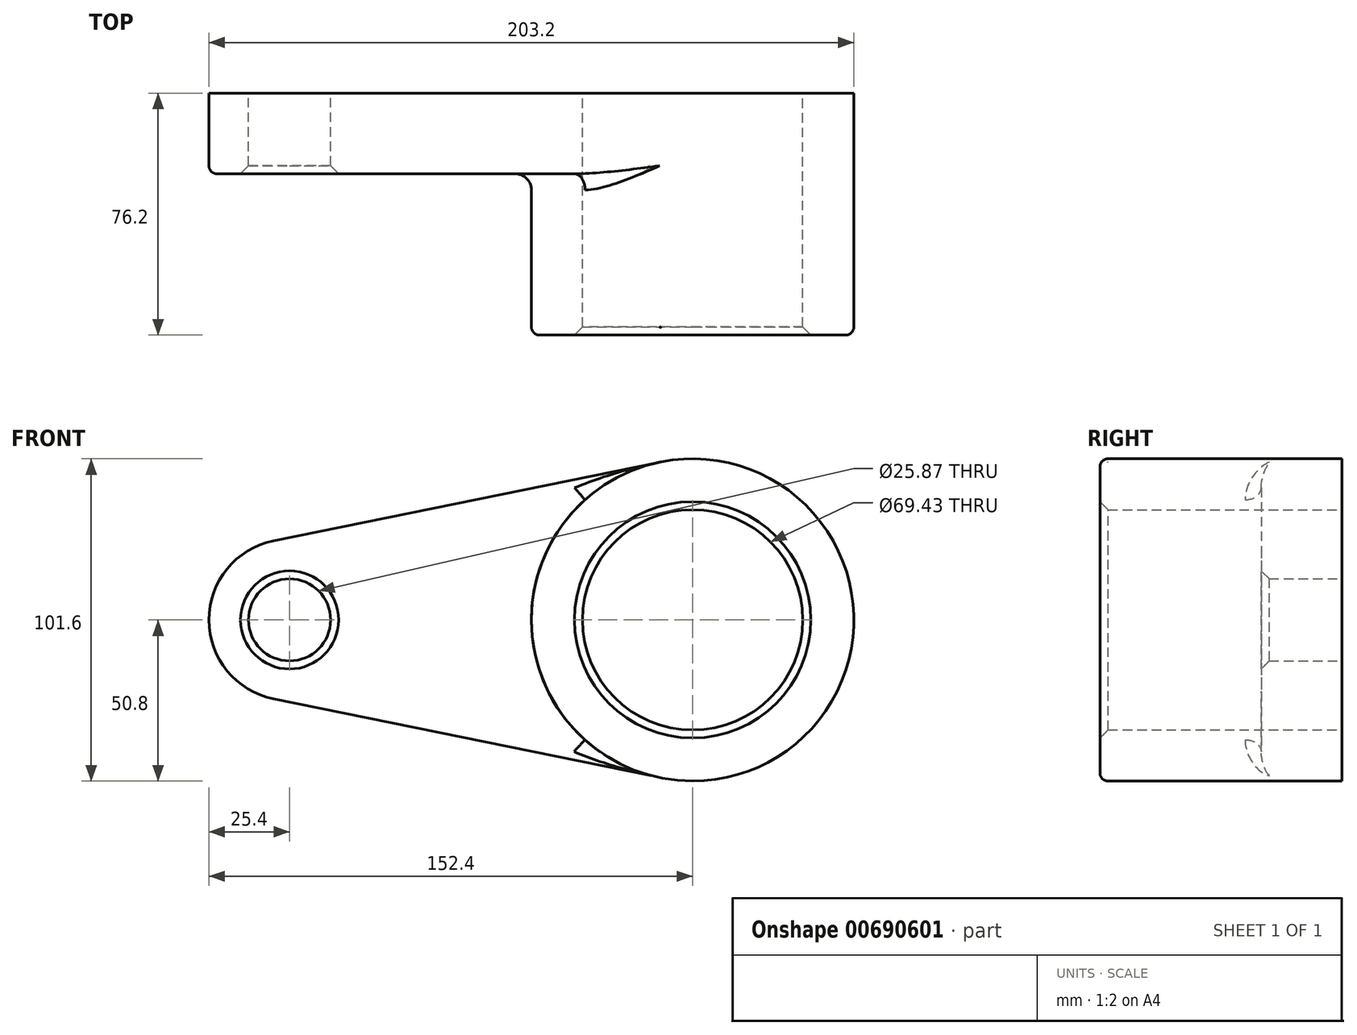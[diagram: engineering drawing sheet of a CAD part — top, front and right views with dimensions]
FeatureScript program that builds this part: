
annotation { "Feature Type Name" : "Feature", "Feature Type Description" : "" }
export const myFeature = defineFeature(function(context is Context, id is Id, definition is map)
    precondition{}
    {
        {
            var Q0;
            Q0=qCreatedBy(makeId("Front.planeOp"),FACE);
            var sketch = newSketch(context, id + "F0", { "sketchPlane" : qUnion([Q0])});
            skCircle(sketch, "E0", {"center": v(0, 0) * mm, "radius": 50.8 * mm});
            skCircle(sketch, "E1", {"center": v(-127, 0) * mm, "radius": 25.4 * mm});
            skLineSegment(sketch, "E2", {"start": v(-13.3, -49.03) * mm, "end": v(-132.06, -24.9) * mm});
            skLineSegment(sketch, "E3", {"start": v(-9.88, 49.83) * mm, "end": v(-132.08, 24.89) * mm});
            skCircle(sketch, "E4", {"center": v(0, 0) * mm, "radius": 34.71 * mm});
            skCircle(sketch, "E5", {"center": v(-127, 0) * mm, "radius": 12.94 * mm});
            skSolve(sketch);
        }
        {
            var Q0;
            Q0 = qSketchRegion(id + "F0", true);
            extrude(context, id + "F1", {"entities" : qUnion([Q0]), "depth" : 25.4 * mm, "offsetDistance" : 25.4 * mm});
        }
        {
            var Q0;
            Q0 = qSketchRegion(id + "F0", true);
            extrude(context, id + "F2", {"entities" : qUnion([Q0]), "operationType" : NewBodyOperationType.REMOVE, "oppositeDirection" : true, "depth" : 76.2 * mm, "offsetDistance" : 25.4 * mm});
        }
        {
            var Q0;
            Q0=makeQuery(id+"F0.imprint","IMPRINT",FACE,{"disambiguationData":[TD([[makeQuery(id+"F0.imprint","IMPRINT",EDGE,{"derivedFrom":sQuery(id+"F0.wireOp",EDGE,"E4")}),-1.0]])]});
            extrude(context, id + "F3", {"entities" : qUnion([Q0]), "operationType" : NewBodyOperationType.ADD, "depth" : 76.2 * mm, "offsetDistance" : 25.4 * mm});
        }
        {
            var Q0;
            Q0=makeQuery(id+"F3.opExtrude","CAP_EDGE",EDGE,{"disambiguationData":[OSD([sQuery(id+"F0.wireOp",EDGE,"E0")])],"isStart":false});
            fillet(context, id + "F4", {"entities" : qUnion([Q0]), "radius" : 2.54 * mm, "tangentPropagation" : true, "allowEdgeOverflow" : false});
        }
        {
            var Q0;
            Q0=makeQuery(id+"F3.opExtrude","CAP_EDGE",EDGE,{"disambiguationData":[OSD([sQuery(id+"F0.wireOp",EDGE,"E4")])],"isStart":false});
            chamfer(context, id + "F5", {"entities" : qUnion([Q0]), "width" : 2.54 * mm, "tangentPropagation" : true});
        }
        {
            var Q0;
            Q0=makeQuery(id+"F1.opExtrude","CAP_EDGE",EDGE,{"disambiguationData":[OSD([sQuery(id+"F0.wireOp",EDGE,"E5")])],"isStart":false});
            chamfer(context, id + "F6", {"entities" : qUnion([Q0]), "width" : 2.54 * mm, "tangentPropagation" : true});
        }
        {
            var Q0;
            Q0=makeQuery(id+"F1.opExtrude","CAP_EDGE",EDGE,{"disambiguationData":[OSD([sQuery(id+"F0.wireOp",EDGE,"E3")])],"isStart":false});
            fillet(context, id + "F7", {"entities" : qUnion([Q0]), "radius" : 2.54 * mm, "tangentPropagation" : true, "allowEdgeOverflow" : false});
        }
        {
            var Q0;
            {var subQ0=sQuery(id+"F0.wireOp",EDGE,"E0");Q0=makeQuery(id+"F3.boolean.opBoolean","INTERSECT",EDGE,{"derivedFrom":[makeQuery(id+"F1.opExtrude","CAP_FACE",FACE,{"disambiguationData":[OSD([subQ0,sQuery(id+"F0.wireOp",EDGE,"E1"),sQuery(id+"F0.wireOp",EDGE,"E2"),sQuery(id+"F0.wireOp",EDGE,"E3"),sQuery(id+"F0.wireOp",EDGE,"E4"),sQuery(id+"F0.wireOp",EDGE,"E5")])],"isStart":false}),makeQuery(id+"F3.opExtrude","SWEPT_FACE",FACE,{"disambiguationData":[OSD([subQ0])]})]});}
            fillet(context, id + "F8", {"entities" : qUnion([Q0]), "radius" : 5.08 * mm, "tangentPropagation" : true, "allowEdgeOverflow" : false});
        }
    });
